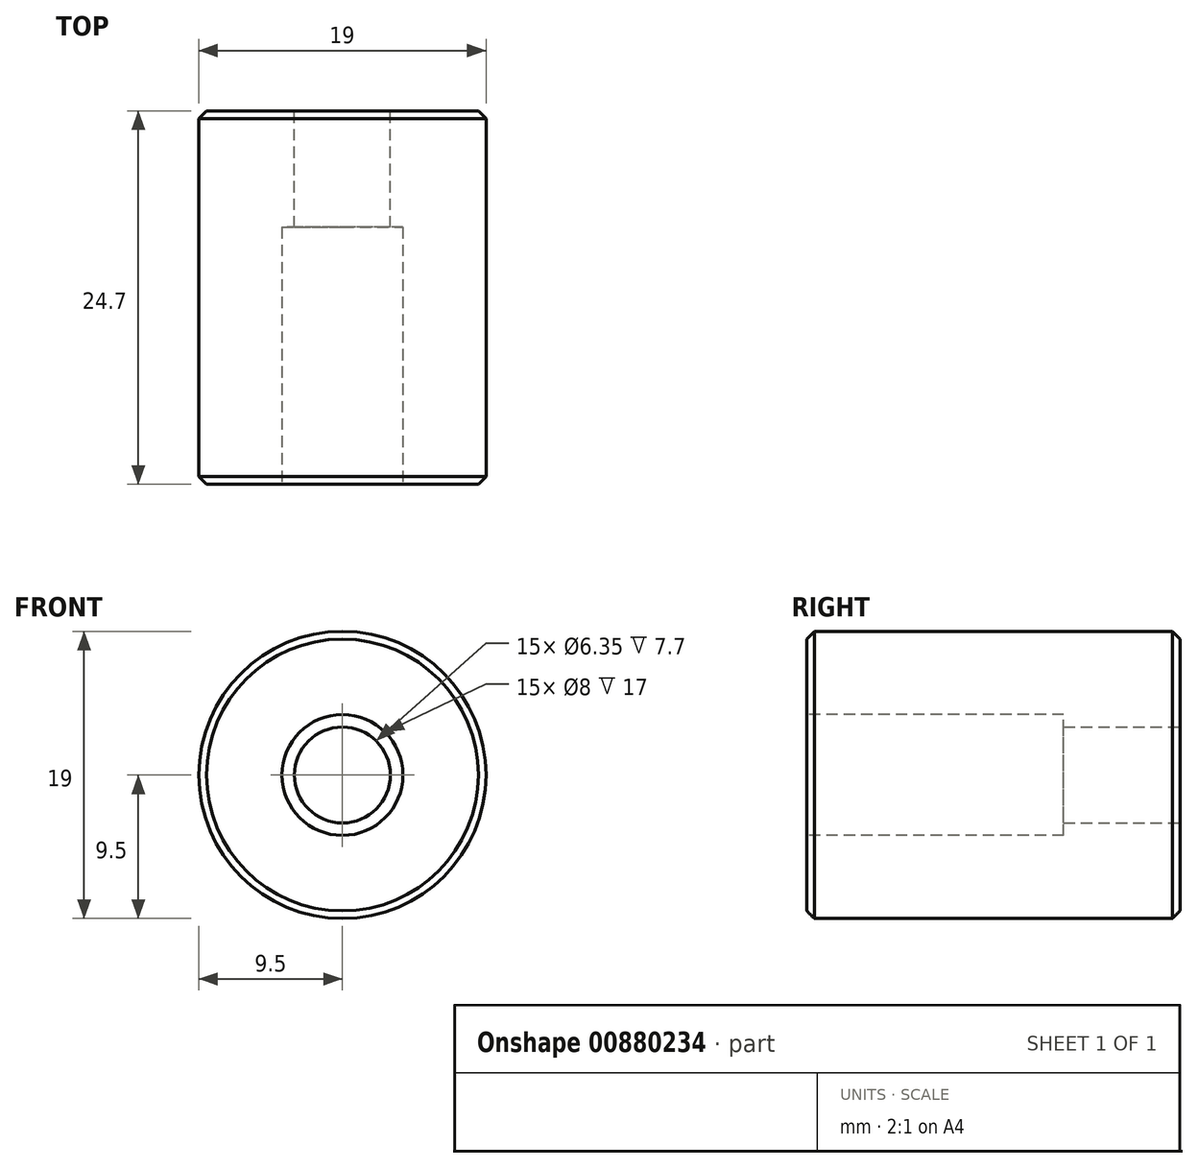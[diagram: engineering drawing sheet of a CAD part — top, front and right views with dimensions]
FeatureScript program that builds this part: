
annotation { "Feature Type Name" : "Feature", "Feature Type Description" : "" }
export const myFeature = defineFeature(function(context is Context, id is Id, definition is map)
    precondition{}
    {
        {
            var Q0;
            Q0=qCreatedBy(makeId("Front.planeOp"),FACE);
            var sketch = newSketch(context, id + "F0", { "sketchPlane" : qUnion([Q0])});
            skCircle(sketch, "E0", {"center": v(0, 0) * mm, "radius": 9.5 * mm});
            skCircle(sketch, "E1", {"center": v(0, 0) * mm, "radius": 3.17 * mm});
            skSolve(sketch);
        }
        {
            var Q0;
            Q0=qSketchRegion(id+"F0",true);
            extrude(context, id + "F1", {"entities" : qUnion([Q0]), "depth" : 24.7 * mm});
        }
        {
            var Q0;
            Q0=makeQuery(id+"F1.opExtrude","CAP_FACE",FACE,{"disambiguationData":[OSD([sQuery(id+"F0.wireOp",EDGE,"E0"),sQuery(id+"F0.wireOp",EDGE,"E1")])],"isStart":false});
            var sketch = newSketch(context, id + "F2", { "sketchPlane" : qUnion([Q0])});
            skCircle(sketch, "E2", {"center": v(0, 0) * mm, "radius": 4 * mm});
            skSolve(sketch);
        }
        {
            var Q0;
            Q0=qSketchRegion(id+"F2",true);
            extrude(context, id + "F3", {"entities" : qUnion([Q0]), "operationType" : NewBodyOperationType.REMOVE, "oppositeDirection" : true, "depth" : 17 * mm});
        }
        {
            var Q0;
            Q0=makeQuery(id+"F1.opExtrude","SWEPT_FACE",FACE,{"disambiguationData":[OSD([sQuery(id+"F0.wireOp",EDGE,"E0")])]});
            chamfer(context, id + "F4", {"entities" : qUnion([Q0]), "width" : 0.5 * mm, "tangentPropagation" : true});
        }
    });
